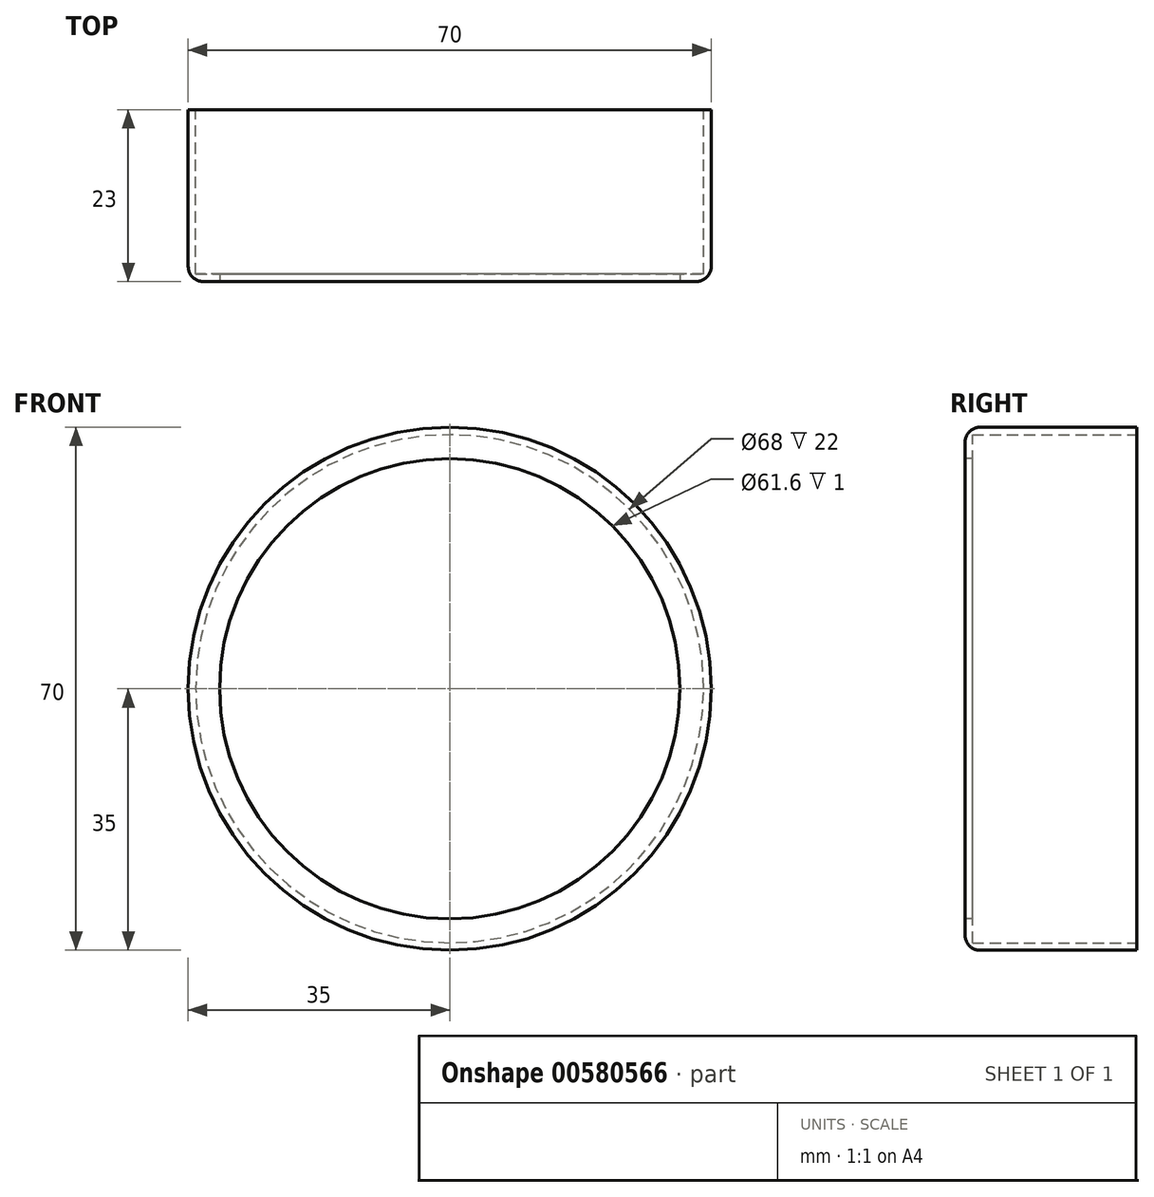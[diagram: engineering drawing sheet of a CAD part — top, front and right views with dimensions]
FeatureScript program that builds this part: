
annotation { "Feature Type Name" : "Feature", "Feature Type Description" : "" }
export const myFeature = defineFeature(function(context is Context, id is Id, definition is map)
    precondition{}
    {
        {
            var Q0;
            Q0=qCreatedBy(makeId("Front.planeOp"),FACE);
            var sketch = newSketch(context, id + "F0", { "sketchPlane" : qUnion([Q0])});
            skCircle(sketch, "E0", {"center": v(0, 0) * mm, "radius": 35 * mm});
            skSolve(sketch);
        }
        {
            var Q0;
            Q0=makeQuery(id+"F0.imprint","IMPRINT",FACE,{"disambiguationData":[TD([[makeQuery(id+"F0.imprint","IMPRINT",EDGE,{"derivedFrom":sQuery(id+"F0.wireOp",EDGE,"E0")}),1.0]])]});
            extrude(context, id + "F1", {"entities" : qUnion([Q0]), "depth" : 23 * mm, "offsetDistance" : 25 * mm});
        }
        {
            var Q0;
            Q0=makeQuery(id+"F1.opExtrude","CAP_FACE",FACE,{"disambiguationData":[OSD([sQuery(id+"F0.wireOp",EDGE,"E0")])],"isStart":true});
            shell(context, id + "F2", {"entities" : qUnion([Q0]), "thickness" : 1 * mm});
        }
        {
            var Q0;
            Q0=makeQuery(id+"F1.opExtrude","CAP_EDGE",EDGE,{"disambiguationData":[OSD([sQuery(id+"F0.wireOp",EDGE,"E0")])],"isStart":false});
            fillet(context, id + "F3", {"entities" : qUnion([Q0]), "radius" : 2 * mm, "tangentPropagation" : true, "allowEdgeOverflow" : false});
        }
        {
            var Q0;
            Q0=makeQuery(id+"F1.opExtrude","CAP_FACE",FACE,{"disambiguationData":[OSD([sQuery(id+"F0.wireOp",EDGE,"E0")])],"isStart":false});
            var sketch = newSketch(context, id + "F4", { "sketchPlane" : qUnion([Q0])});
            skCircle(sketch, "E1", {"center": v(0, 0) * mm, "radius": 30.8 * mm});
            skSolve(sketch);
        }
        {
            var Q0;
            Q0=makeQuery(id+"F4.imprint","IMPRINT",FACE,{"disambiguationData":[TD([[makeQuery(id+"F4.imprint","IMPRINT",EDGE,{"derivedFrom":sQuery(id+"F4.wireOp",EDGE,"E1")}),1.0]])]});
            extrude(context, id + "F5", {"entities" : qUnion([Q0]), "operationType" : NewBodyOperationType.REMOVE, "oppositeDirection" : true, "depth" : 1 * mm, "offsetDistance" : 25 * mm});
        }
    });
